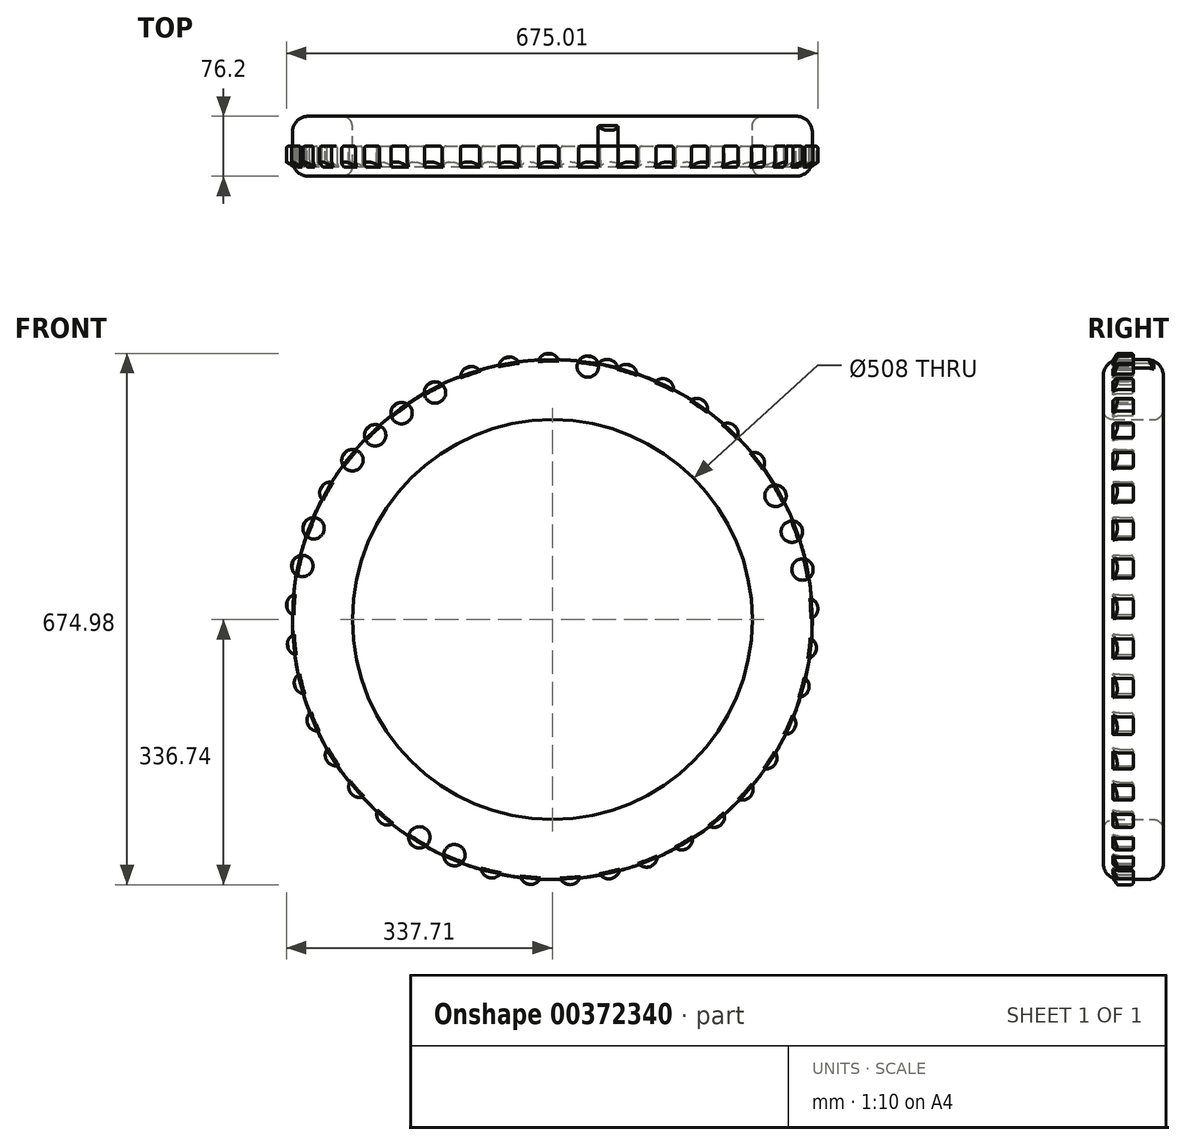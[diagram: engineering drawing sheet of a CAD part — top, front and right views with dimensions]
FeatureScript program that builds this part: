
annotation { "Feature Type Name" : "Feature", "Feature Type Description" : "" }
export const myFeature = defineFeature(function(context is Context, id is Id, definition is map)
    precondition{}
    {
        {
            var Q0;
            Q0=qCreatedBy(makeId("Front.planeOp"),FACE);
            var sketch = newSketch(context, id + "F0", { "sketchPlane" : qUnion([Q0])});
            skCircle(sketch, "E0", {"center": v(0, 0) * mm, "radius": 330.2 * mm});
            skCircle(sketch, "E1", {"center": v(0, 0) * mm, "radius": 254 * mm});
            skSolve(sketch);
        }
        {
            var Q0;
            Q0 = qSketchRegion(id + "F0", true);
            extrude(context, id + "F1", {"entities" : qUnion([Q0]), "endBound" : BoundingType.SYMMETRIC, "depth" : 76.2 * mm});
        }
        {
            var Q0;
            Q0=makeQuery(id+"F1.opExtrude","CAP_EDGE",EDGE,{"disambiguationData":[OSD([sQuery(id+"F0.wireOp",EDGE,"E0")])],"isStart":false});
            var Q1;
            Q1=makeQuery(id+"F1.opExtrude","CAP_EDGE",EDGE,{"disambiguationData":[OSD([sQuery(id+"F0.wireOp",EDGE,"E0")])],"isStart":true});
            fillet(context, id + "F2", {"entities" : qUnion([Q0, Q1]), "radius" : 20.32 * mm, "tangentPropagation" : true, "allowEdgeOverflow" : false});
        }
        {
            var Q0;
            Q0=qCreatedBy(makeId("Front.planeOp"),FACE);
            var sketch = newSketch(context, id + "F3", { "sketchPlane" : qUnion([Q0])});
            skLineSegment(sketch, "E2", {"start": v(-204.7, 258.7) * mm, "end": v(-200.7, 257.56) * mm});
            skLineSegment(sketch, "E3.MirrorCS", {"start": v(-184.2, 273.67) * mm, "end": v(-184.34, 269.52) * mm});
            skLineSegment(sketch, "E4", {"start": v(-184.34, 269.52) * mm, "end": v(-200.7, 257.56) * mm});
            skArc(sketch, "E5", {"start": v(-184.2, 273.67) * mm, "mid": v(-199.59, 273.22) * mm, "end": v(-204.7, 258.7) * mm});
            skLineSegment(sketch, "E6.MirrorCS", {"start": v(-158.8, 285.3) * mm, "end": v(-140.8, 294.6) * mm});
            skLineSegment(sketch, "E7.MirrorCS", {"start": v(-162.58, 287.04) * mm, "end": v(-158.8, 285.3) * mm});
            skArc(sketch, "E8.MirrorCS", {"start": v(-162.58, 287.04) * mm, "mid": v(-155.3, 300.6) * mm, "end": v(-140.03, 298.69) * mm});
            skLineSegment(sketch, "E9.MirrorCS", {"start": v(-140.03, 298.69) * mm, "end": v(-140.8, 294.6) * mm});
            skArc(sketch, "E10.MirrorCS", {"start": v(-92.54, 316.62) * mm, "mid": v(-107.34, 320.86) * mm, "end": v(-116.6, 308.58) * mm});
            skLineSegment(sketch, "E11.MirrorCS", {"start": v(-116.6, 308.58) * mm, "end": v(-113.14, 306.28) * mm});
            skLineSegment(sketch, "E12.MirrorCS", {"start": v(-93.93, 312.7) * mm, "end": v(-113.14, 306.28) * mm});
            skLineSegment(sketch, "E13.MirrorCS", {"start": v(-92.54, 316.62) * mm, "end": v(-93.93, 312.7) * mm});
            skLineSegment(sketch, "E14.MirrorCS", {"start": v(-64.8, 320) * mm, "end": v(-44.83, 323.38) * mm});
            skArc(sketch, "E15.MirrorCS", {"start": v(-67.88, 322.8) * mm, "mid": v(-56.82, 333.5) * mm, "end": v(-42.86, 327.04) * mm});
            skLineSegment(sketch, "E16.MirrorCS", {"start": v(-67.88, 322.8) * mm, "end": v(-64.8, 320) * mm});
            skLineSegment(sketch, "E17.MirrorCS", {"start": v(-42.86, 327.04) * mm, "end": v(-44.83, 323.38) * mm});
            skArc(sketch, "E18.MirrorCS", {"start": v(7.84, 329.7) * mm, "mid": v(-4.97, 338.24) * mm, "end": v(-17.54, 329.35) * mm});
            skLineSegment(sketch, "E19.MirrorCS", {"start": v(5.32, 326.4) * mm, "end": v(-14.93, 326.11) * mm});
            skLineSegment(sketch, "E20.MirrorCS", {"start": v(-17.54, 329.35) * mm, "end": v(-14.93, 326.11) * mm});
            skLineSegment(sketch, "E21.MirrorCS", {"start": v(7.84, 329.7) * mm, "end": v(5.32, 326.4) * mm});
            skArc(sketch, "E22.MirrorCS", {"start": v(33.21, 328.1) * mm, "mid": v(47, 334.94) * mm, "end": v(58.34, 324.54) * mm});
            skLineSegment(sketch, "E23.MirrorCS", {"start": v(58.34, 324.54) * mm, "end": v(55.35, 321.65) * mm});
            skLineSegment(sketch, "E24.MirrorCS", {"start": v(35.29, 324.49) * mm, "end": v(55.35, 321.65) * mm});
            skLineSegment(sketch, "E25.MirrorCS", {"start": v(33.21, 328.1) * mm, "end": v(35.29, 324.49) * mm});
            skArc(sketch, "E26.MirrorCS", {"start": v(107.45, 311.67) * mm, "mid": v(97.84, 323.7) * mm, "end": v(83.17, 319.05) * mm});
            skLineSegment(sketch, "E27.MirrorCS", {"start": v(104.05, 309.28) * mm, "end": v(84.66, 315.17) * mm});
            skLineSegment(sketch, "E28.MirrorCS", {"start": v(83.17, 319.05) * mm, "end": v(84.66, 315.17) * mm});
            skLineSegment(sketch, "E29.MirrorCS", {"start": v(107.45, 311.67) * mm, "end": v(104.05, 309.28) * mm});
            skArc(sketch, "E30.MirrorCS", {"start": v(131.14, 302.43) * mm, "mid": v(146.35, 304.77) * mm, "end": v(154, 291.42) * mm});
            skArc(sketch, "E31.MirrorCS", {"start": v(196.87, 264.24) * mm, "mid": v(191.37, 278.62) * mm, "end": v(175.98, 278.64) * mm});
            skArc(sketch, "E32.MirrorCS", {"start": v(216.64, 248.24) * mm, "mid": v(231.84, 245.85) * mm, "end": v(235.07, 230.8) * mm});
            skLineSegment(sketch, "E33.MirrorCS", {"start": v(216.24, 244.1) * mm, "end": v(230.96, 230.18) * mm});
            skLineSegment(sketch, "E34.MirrorCS", {"start": v(192.9, 263) * mm, "end": v(176.23, 274.5) * mm});
            skLineSegment(sketch, "E35.MirrorCS", {"start": v(132.02, 298.37) * mm, "end": v(150.27, 289.57) * mm});
            skLineSegment(sketch, "E36.MirrorCS", {"start": v(235.07, 230.8) * mm, "end": v(230.96, 230.18) * mm});
            skLineSegment(sketch, "E37.MirrorCS", {"start": v(216.64, 248.24) * mm, "end": v(216.24, 244.1) * mm});
            skLineSegment(sketch, "E38.MirrorCS", {"start": v(196.87, 264.24) * mm, "end": v(192.9, 263) * mm});
            skLineSegment(sketch, "E39.MirrorCS", {"start": v(175.98, 278.64) * mm, "end": v(176.23, 274.5) * mm});
            skLineSegment(sketch, "E40.MirrorCS", {"start": v(154, 291.42) * mm, "end": v(150.27, 289.57) * mm});
            skLineSegment(sketch, "E41.MirrorCS", {"start": v(131.14, 302.43) * mm, "end": v(132.02, 298.37) * mm});
            skLineSegment(sketch, "E42.MirrorCS", {"start": v(249.43, -209.24) * mm, "end": v(235.92, -224.34) * mm});
            skArc(sketch, "E43.MirrorCS", {"start": v(253.57, -209.51) * mm, "mid": v(251.61, -224.78) * mm, "end": v(236.66, -228.43) * mm});
            skLineSegment(sketch, "E44.MirrorCS", {"start": v(236.66, -228.43) * mm, "end": v(235.92, -224.34) * mm});
            skLineSegment(sketch, "E45.MirrorCS", {"start": v(253.57, -209.51) * mm, "end": v(249.43, -209.24) * mm});
            skArc(sketch, "E46.MirrorCS", {"start": v(269.01, -189.3) * mm, "mid": v(283.22, -183.4) * mm, "end": v(282.82, -168.02) * mm});
            skLineSegment(sketch, "E47.MirrorCS", {"start": v(267.65, -185.38) * mm, "end": v(278.68, -168.38) * mm});
            skLineSegment(sketch, "E48.MirrorCS", {"start": v(269.01, -189.3) * mm, "end": v(267.65, -185.38) * mm});
            skLineSegment(sketch, "E49.MirrorCS", {"start": v(282.82, -168.02) * mm, "end": v(278.68, -168.38) * mm});
            skArc(sketch, "E50.MirrorCS", {"start": v(305.33, -122.52) * mm, "mid": v(308.1, -137.66) * mm, "end": v(294.96, -145.68) * mm});
            skLineSegment(sketch, "E51.MirrorCS", {"start": v(301.3, -123.52) * mm, "end": v(293.02, -142) * mm});
            skLineSegment(sketch, "E52.MirrorCS", {"start": v(305.33, -122.52) * mm, "end": v(301.3, -123.52) * mm});
            skLineSegment(sketch, "E53.MirrorCS", {"start": v(294.96, -145.68) * mm, "end": v(293.02, -142) * mm});
            skArc(sketch, "E54.MirrorCS", {"start": v(313.9, -98.58) * mm, "mid": v(325.65, -88.64) * mm, "end": v(320.6, -74.1) * mm});
            skArc(sketch, "E55.MirrorCS", {"start": v(328.22, -23.92) * mm, "mid": v(335.46, -37.5) * mm, "end": v(325.38, -49.13) * mm});
            skArc(sketch, "E56.MirrorCS", {"start": v(329.12, 1.5) * mm, "mid": v(337.29, 14.54) * mm, "end": v(328.05, 26.85) * mm});
            skArc(sketch, "E57.MirrorCS", {"start": v(320.08, 76.98) * mm, "mid": v(331.1, 66.24) * mm, "end": v(325.03, 52.1) * mm});
            skLineSegment(sketch, "E58.MirrorCS", {"start": v(325.03, 52.1) * mm, "end": v(321.32, 53.97) * mm});
            skLineSegment(sketch, "E59.MirrorCS", {"start": v(317.37, 73.84) * mm, "end": v(321.32, 53.97) * mm});
            skLineSegment(sketch, "E60.MirrorCS", {"start": v(311.42, -95.25) * mm, "end": v(316.76, -75.7) * mm});
            skLineSegment(sketch, "E61.MirrorCS", {"start": v(320.6, -74.1) * mm, "end": v(316.76, -75.7) * mm});
            skLineSegment(sketch, "E62.MirrorCS", {"start": v(313.9, -98.58) * mm, "end": v(311.42, -95.25) * mm});
            skLineSegment(sketch, "E63.MirrorCS", {"start": v(325.38, -49.13) * mm, "end": v(322.41, -46.22) * mm});
            skLineSegment(sketch, "E64.MirrorCS", {"start": v(324.68, -26.1) * mm, "end": v(322.41, -46.22) * mm});
            skLineSegment(sketch, "E65.MirrorCS", {"start": v(328.22, -23.92) * mm, "end": v(324.68, -26.1) * mm});
            skLineSegment(sketch, "E66.MirrorCS", {"start": v(328.05, 26.85) * mm, "end": v(324.89, 24.16) * mm});
            skLineSegment(sketch, "E67.MirrorCS", {"start": v(320.08, 76.98) * mm, "end": v(317.37, 73.84) * mm});
            skArc(sketch, "E68.MirrorCS", {"start": v(313.22, 101.47) * mm, "mid": v(317.04, 116.37) * mm, "end": v(304.5, 125.3) * mm});
            skLineSegment(sketch, "E69.MirrorCS", {"start": v(313.22, 101.47) * mm, "end": v(309.26, 102.74) * mm});
            skLineSegment(sketch, "E70.MirrorCS", {"start": v(309.26, 102.74) * mm, "end": v(302.3, 121.77) * mm});
            skLineSegment(sketch, "E71.MirrorCS", {"start": v(304.5, 125.3) * mm, "end": v(302.3, 121.77) * mm});
            skArc(sketch, "E72.MirrorCS", {"start": v(281.68, 170.64) * mm, "mid": v(295.44, 163.75) * mm, "end": v(293.95, 148.43) * mm});
            skLineSegment(sketch, "E73.MirrorCS", {"start": v(293.95, 148.43) * mm, "end": v(289.85, 149.09) * mm});
            skLineSegment(sketch, "E74.MirrorCS", {"start": v(280.05, 166.82) * mm, "end": v(289.85, 149.09) * mm});
            skLineSegment(sketch, "E75.MirrorCS", {"start": v(281.68, 170.64) * mm, "end": v(280.05, 166.82) * mm});
            skArc(sketch, "E76.MirrorCS", {"start": v(267.7, 191.88) * mm, "mid": v(266.81, 207.25) * mm, "end": v(252.16, 211.94) * mm});
            skLineSegment(sketch, "E77.MirrorCS", {"start": v(252.16, 211.94) * mm, "end": v(251.13, 207.91) * mm});
            skLineSegment(sketch, "E78.MirrorCS", {"start": v(263.54, 191.9) * mm, "end": v(251.13, 207.91) * mm});
            skLineSegment(sketch, "E79.MirrorCS", {"start": v(267.7, 191.88) * mm, "end": v(263.54, 191.9) * mm});
            skArc(sketch, "E80.MirrorCS", {"start": v(-279.9, 174.58) * mm, "mid": v(-293.75, 167.88) * mm, "end": v(-292.48, 152.54) * mm});
            skArc(sketch, "E81.MirrorCS", {"start": v(-265.62, 195.62) * mm, "mid": v(-264.52, 210.97) * mm, "end": v(-249.8, 215.46) * mm});
            skArc(sketch, "E82.MirrorCS", {"start": v(-312.4, 105.85) * mm, "mid": v(-316.01, 120.8) * mm, "end": v(-303.35, 129.55) * mm});
            skArc(sketch, "E83.MirrorCS", {"start": v(-319.6, 81.46) * mm, "mid": v(-330.78, 70.87) * mm, "end": v(-324.9, 56.65) * mm});
            skArc(sketch, "E84.MirrorCS", {"start": v(-329.7, 6.1) * mm, "mid": v(-337.69, 19.26) * mm, "end": v(-328.28, 31.44) * mm});
            skArc(sketch, "E85.MirrorCS", {"start": v(-329.16, -19.31) * mm, "mid": v(-336.58, -32.8) * mm, "end": v(-326.67, -44.56) * mm});
            skArc(sketch, "E86.MirrorCS", {"start": v(-315.89, -94.17) * mm, "mid": v(-327.5, -84.06) * mm, "end": v(-322.23, -69.6) * mm});
            skArc(sketch, "E87.MirrorCS", {"start": v(-307.65, -118.23) * mm, "mid": v(-310.63, -133.33) * mm, "end": v(-297.61, -141.53) * mm});
            skArc(sketch, "E88.MirrorCS", {"start": v(-272.27, -185.52) * mm, "mid": v(-286.4, -179.41) * mm, "end": v(-285.78, -164.04) * mm});
            skArc(sketch, "E89.MirrorCS", {"start": v(-257.12, -205.94) * mm, "mid": v(-255.37, -221.23) * mm, "end": v(-240.47, -225.1) * mm});
            skArc(sketch, "E90.MirrorCS", {"start": v(-202.96, -259.33) * mm, "mid": v(-218.28, -257.8) * mm, "end": v(-222.35, -242.96) * mm});
            skArc(sketch, "E91.MirrorCS", {"start": v(-182.33, -274.2) * mm, "mid": v(-176.03, -288.23) * mm, "end": v(-160.66, -287.4) * mm});
            skArc(sketch, "E92.MirrorCS", {"start": v(-114.54, -308.62) * mm, "mid": v(-129.6, -311.81) * mm, "end": v(-137.99, -298.9) * mm});
            skArc(sketch, "E93.MirrorCS", {"start": v(-90.37, -316.51) * mm, "mid": v(-80.1, -327.98) * mm, "end": v(-65.72, -322.5) * mm});
            skArc(sketch, "E94.MirrorCS", {"start": v(-15.33, -328.73) * mm, "mid": v(-28.7, -336.34) * mm, "end": v(-40.62, -326.6) * mm});
            skArc(sketch, "E95.MirrorCS", {"start": v(10.1, -328.9) * mm, "mid": v(23.36, -336.7) * mm, "end": v(35.4, -327.12) * mm});
            skArc(sketch, "E96.MirrorCS", {"start": v(85.3, -317.74) * mm, "mid": v(74.87, -329.06) * mm, "end": v(60.56, -323.4) * mm});
            skArc(sketch, "E97.MirrorCS", {"start": v(109.58, -310.2) * mm, "mid": v(124.59, -313.6) * mm, "end": v(133.15, -300.8) * mm});
            skArc(sketch, "E98.MirrorCS", {"start": v(177.84, -276.72) * mm, "mid": v(171.34, -290.67) * mm, "end": v(155.98, -289.61) * mm});
            skArc(sketch, "E99.MirrorCS", {"start": v(198.68, -262.15) * mm, "mid": v(214, -260.83) * mm, "end": v(218.29, -246.04) * mm});
            skLineSegment(sketch, "E100.MirrorCS", {"start": v(329.12, 1.5) * mm, "end": v(325.74, 3.91) * mm});
            skLineSegment(sketch, "E101", {"start": v(324.89, 24.16) * mm, "end": v(325.74, 3.91) * mm});
            skArc(sketch, "E102.MirrorCS", {"start": v(-237.61, 228.84) * mm, "mid": v(-234.5, 243.91) * mm, "end": v(-219.32, 246.42) * mm});
            skLineSegment(sketch, "E103.MirrorCS", {"start": v(-233.5, 228.25) * mm, "end": v(-218.9, 242.29) * mm});
            skLineSegment(sketch, "E104.MirrorCS", {"start": v(-237.61, 228.84) * mm, "end": v(-233.5, 228.25) * mm});
            skLineSegment(sketch, "E105.MirrorCS", {"start": v(-219.32, 246.42) * mm, "end": v(-218.9, 242.29) * mm});
            skLineSegment(sketch, "E106.MirrorCS", {"start": v(-265.62, 195.62) * mm, "end": v(-261.46, 195.58) * mm});
            skLineSegment(sketch, "E107.MirrorCS", {"start": v(-261.46, 195.58) * mm, "end": v(-248.83, 211.41) * mm});
            skLineSegment(sketch, "E108.MirrorCS", {"start": v(-249.8, 215.46) * mm, "end": v(-248.83, 211.41) * mm});
            skLineSegment(sketch, "E109.MirrorCS", {"start": v(-292.48, 152.54) * mm, "end": v(-288.37, 153.14) * mm});
            skLineSegment(sketch, "E110.MirrorCS", {"start": v(-278.32, 170.73) * mm, "end": v(-288.37, 153.14) * mm});
            skLineSegment(sketch, "E111.MirrorCS", {"start": v(-279.9, 174.58) * mm, "end": v(-278.32, 170.73) * mm});
            skLineSegment(sketch, "E112.MirrorCS", {"start": v(-303.35, 129.55) * mm, "end": v(-301.2, 126) * mm});
            skLineSegment(sketch, "E113.MirrorCS", {"start": v(-308.43, 107.07) * mm, "end": v(-301.2, 126) * mm});
            skLineSegment(sketch, "E114.MirrorCS", {"start": v(-312.4, 105.85) * mm, "end": v(-308.43, 107.07) * mm});
            skLineSegment(sketch, "E115.MirrorCS", {"start": v(-319.6, 81.46) * mm, "end": v(-316.94, 78.28) * mm});
            skLineSegment(sketch, "E116.MirrorCS", {"start": v(-316.94, 78.28) * mm, "end": v(-321.17, 58.47) * mm});
            skLineSegment(sketch, "E117.MirrorCS", {"start": v(-324.9, 56.65) * mm, "end": v(-321.17, 58.47) * mm});
            skLineSegment(sketch, "E118.MirrorCS", {"start": v(-328.28, 31.44) * mm, "end": v(-325.15, 28.7) * mm});
            skLineSegment(sketch, "E119.MirrorCS", {"start": v(-326.29, 8.48) * mm, "end": v(-325.15, 28.7) * mm});
            skLineSegment(sketch, "E120.MirrorCS", {"start": v(-329.7, 6.1) * mm, "end": v(-326.29, 8.48) * mm});
            skLineSegment(sketch, "E121.MirrorCS", {"start": v(-329.16, -19.31) * mm, "end": v(-325.65, -21.54) * mm});
            skLineSegment(sketch, "E122.MirrorCS", {"start": v(-325.65, -21.54) * mm, "end": v(-323.66, -41.7) * mm});
            skLineSegment(sketch, "E123.MirrorCS", {"start": v(-326.67, -44.56) * mm, "end": v(-323.66, -41.7) * mm});
            skLineSegment(sketch, "E124.MirrorCS", {"start": v(-322.23, -69.6) * mm, "end": v(-318.42, -71.26) * mm});
            skLineSegment(sketch, "E125.MirrorCS", {"start": v(-313.36, -90.88) * mm, "end": v(-318.42, -71.26) * mm});
            skLineSegment(sketch, "E126.MirrorCS", {"start": v(-315.89, -94.17) * mm, "end": v(-313.36, -90.88) * mm});
            skLineSegment(sketch, "E127.MirrorCS", {"start": v(-307.65, -118.23) * mm, "end": v(-303.63, -119.28) * mm});
            skLineSegment(sketch, "E128.MirrorCS", {"start": v(-303.63, -119.28) * mm, "end": v(-295.61, -137.89) * mm});
            skLineSegment(sketch, "E129.MirrorCS", {"start": v(-297.61, -141.53) * mm, "end": v(-295.61, -137.89) * mm});
            skLineSegment(sketch, "E130.MirrorCS", {"start": v(-285.78, -164.04) * mm, "end": v(-281.64, -164.46) * mm});
            skLineSegment(sketch, "E131.MirrorCS", {"start": v(-270.86, -181.6) * mm, "end": v(-281.64, -164.46) * mm});
            skLineSegment(sketch, "E132.MirrorCS", {"start": v(-272.27, -185.52) * mm, "end": v(-270.86, -181.6) * mm});
            skLineSegment(sketch, "E133.MirrorCS", {"start": v(-257.12, -205.94) * mm, "end": v(-252.97, -205.72) * mm});
            skLineSegment(sketch, "E134.MirrorCS", {"start": v(-252.97, -205.72) * mm, "end": v(-239.68, -221) * mm});
            skLineSegment(sketch, "E135.MirrorCS", {"start": v(-240.47, -225.1) * mm, "end": v(-239.68, -221) * mm});
            skLineSegment(sketch, "E136.MirrorCS", {"start": v(-222.35, -242.96) * mm, "end": v(-218.28, -242.1) * mm});
            skLineSegment(sketch, "E137.MirrorCS", {"start": v(-202.8, -255.18) * mm, "end": v(-218.28, -242.1) * mm});
            skLineSegment(sketch, "E138.MirrorCS", {"start": v(-202.96, -259.33) * mm, "end": v(-202.8, -255.18) * mm});
            skLineSegment(sketch, "E139.MirrorCS", {"start": v(-182.33, -274.2) * mm, "end": v(-178.44, -272.73) * mm});
            skLineSegment(sketch, "E140.MirrorCS", {"start": v(-178.44, -272.73) * mm, "end": v(-161.14, -283.27) * mm});
            skLineSegment(sketch, "E141.MirrorCS", {"start": v(-160.66, -287.4) * mm, "end": v(-161.14, -283.27) * mm});
            skLineSegment(sketch, "E142.MirrorCS", {"start": v(-137.99, -298.9) * mm, "end": v(-134.37, -296.86) * mm});
            skLineSegment(sketch, "E143.MirrorCS", {"start": v(-115.65, -304.62) * mm, "end": v(-134.37, -296.86) * mm});
            skLineSegment(sketch, "E144.MirrorCS", {"start": v(-114.54, -308.62) * mm, "end": v(-115.65, -304.62) * mm});
            skLineSegment(sketch, "E145.MirrorCS", {"start": v(-90.37, -316.51) * mm, "end": v(-87.11, -313.94) * mm});
            skLineSegment(sketch, "E146.MirrorCS", {"start": v(-87.11, -313.94) * mm, "end": v(-67.43, -318.72) * mm});
            skLineSegment(sketch, "E147.MirrorCS", {"start": v(-65.72, -322.5) * mm, "end": v(-67.43, -318.72) * mm});
            skLineSegment(sketch, "E148.MirrorCS", {"start": v(-40.62, -326.6) * mm, "end": v(-37.8, -323.54) * mm});
            skLineSegment(sketch, "E149.MirrorCS", {"start": v(-37.8, -323.54) * mm, "end": v(-17.6, -325.25) * mm});
            skLineSegment(sketch, "E150.MirrorCS", {"start": v(-15.33, -328.73) * mm, "end": v(-17.6, -325.25) * mm});
            skLineSegment(sketch, "E151.MirrorCS", {"start": v(10.1, -328.9) * mm, "end": v(12.42, -325.46) * mm});
            skLineSegment(sketch, "E152.MirrorCS", {"start": v(12.42, -325.46) * mm, "end": v(32.63, -324.04) * mm});
            skLineSegment(sketch, "E153.MirrorCS", {"start": v(35.4, -327.12) * mm, "end": v(32.63, -324.04) * mm});
            skLineSegment(sketch, "E154.MirrorCS", {"start": v(60.56, -323.4) * mm, "end": v(62.32, -319.63) * mm});
            skLineSegment(sketch, "E155.MirrorCS", {"start": v(82.07, -315.12) * mm, "end": v(62.32, -319.63) * mm});
            skLineSegment(sketch, "E156.MirrorCS", {"start": v(85.3, -317.74) * mm, "end": v(82.07, -315.12) * mm});
            skLineSegment(sketch, "E157.MirrorCS", {"start": v(109.58, -310.2) * mm, "end": v(110.74, -306.2) * mm});
            skLineSegment(sketch, "E158.MirrorCS", {"start": v(110.74, -306.2) * mm, "end": v(129.56, -298.7) * mm});
            skLineSegment(sketch, "E159.MirrorCS", {"start": v(133.15, -300.8) * mm, "end": v(129.56, -298.7) * mm});
            skLineSegment(sketch, "E160.MirrorCS", {"start": v(155.98, -289.61) * mm, "end": v(156.52, -285.5) * mm});
            skLineSegment(sketch, "E161.MirrorCS", {"start": v(173.97, -275.2) * mm, "end": v(156.52, -285.5) * mm});
            skLineSegment(sketch, "E162.MirrorCS", {"start": v(177.84, -276.72) * mm, "end": v(173.97, -275.2) * mm});
            skLineSegment(sketch, "E163.MirrorCS", {"start": v(198.68, -262.15) * mm, "end": v(198.57, -257.99) * mm});
            skLineSegment(sketch, "E164.MirrorCS", {"start": v(198.57, -257.99) * mm, "end": v(214.23, -245.14) * mm});
            skLineSegment(sketch, "E165.MirrorCS", {"start": v(218.29, -246.04) * mm, "end": v(214.23, -245.14) * mm});
            skSolve(sketch);
        }
        {
            var Q0;
            Q0 = qSketchRegion(id + "F3", true);
            extrude(context, id + "F4", {"entities" : qUnion([Q0]), "operationType" : NewBodyOperationType.ADD, "depth" : 20.32 * mm});
        }
        {
            var Q0;
            {var subQ0=sQuery(id+"F0.wireOp",EDGE,"E0");Q0=makeQuery(id+"F4.boolean.opBoolean","INTERSECT",EDGE,{"derivedFrom":[makeQuery(id+"F2.opFillet","BLEND_FACE",FACE,{"disambiguationData":[OSD([subQ0]),TDD([makeQuery(id+"F1.opExtrude","CAP_EDGE",EDGE,{"disambiguationData":[OSD([subQ0])],"isStart":false})])]}),makeQuery(id+"F4.opExtrude","CAP_FACE",FACE,{"disambiguationData":[OSD([sQuery(id+"F3.wireOp",EDGE,"E2"),sQuery(id+"F3.wireOp",EDGE,"E3.MirrorCS"),sQuery(id+"F3.wireOp",EDGE,"E4"),sQuery(id+"F3.wireOp",EDGE,"E5")])],"isStart":false})]});}
            var Q1;
            {var subQ0=sQuery(id+"F0.wireOp",EDGE,"E0");Q1=makeQuery(id+"F4.boolean.opBoolean","INTERSECT",EDGE,{"derivedFrom":[makeQuery(id+"F2.opFillet","BLEND_FACE",FACE,{"disambiguationData":[OSD([subQ0]),TDD([makeQuery(id+"F1.opExtrude","CAP_EDGE",EDGE,{"disambiguationData":[OSD([subQ0])],"isStart":false})])]}),makeQuery(id+"F4.opExtrude","CAP_FACE",FACE,{"disambiguationData":[OSD([sQuery(id+"F3.wireOp",EDGE,"E6.MirrorCS"),sQuery(id+"F3.wireOp",EDGE,"E7.MirrorCS"),sQuery(id+"F3.wireOp",EDGE,"E8.MirrorCS"),sQuery(id+"F3.wireOp",EDGE,"E9.MirrorCS")])],"isStart":false})]});}
            var Q2;
            {var subQ0=sQuery(id+"F0.wireOp",EDGE,"E0");Q2=makeQuery(id+"F4.boolean.opBoolean","INTERSECT",EDGE,{"derivedFrom":[makeQuery(id+"F2.opFillet","BLEND_FACE",FACE,{"disambiguationData":[OSD([subQ0]),TDD([makeQuery(id+"F1.opExtrude","CAP_EDGE",EDGE,{"disambiguationData":[OSD([subQ0])],"isStart":false})])]}),makeQuery(id+"F4.opExtrude","CAP_FACE",FACE,{"disambiguationData":[OSD([sQuery(id+"F3.wireOp",EDGE,"E10.MirrorCS"),sQuery(id+"F3.wireOp",EDGE,"E11.MirrorCS"),sQuery(id+"F3.wireOp",EDGE,"E12.MirrorCS"),sQuery(id+"F3.wireOp",EDGE,"E13.MirrorCS")])],"isStart":false})]});}
            var Q3;
            {var subQ0=sQuery(id+"F0.wireOp",EDGE,"E0");Q3=makeQuery(id+"F4.boolean.opBoolean","INTERSECT",EDGE,{"derivedFrom":[makeQuery(id+"F2.opFillet","BLEND_FACE",FACE,{"disambiguationData":[OSD([subQ0]),TDD([makeQuery(id+"F1.opExtrude","CAP_EDGE",EDGE,{"disambiguationData":[OSD([subQ0])],"isStart":false})])]}),makeQuery(id+"F4.opExtrude","CAP_FACE",FACE,{"disambiguationData":[OSD([sQuery(id+"F3.wireOp",EDGE,"E14.MirrorCS"),sQuery(id+"F3.wireOp",EDGE,"E15.MirrorCS"),sQuery(id+"F3.wireOp",EDGE,"E16.MirrorCS"),sQuery(id+"F3.wireOp",EDGE,"E17.MirrorCS")])],"isStart":false})]});}
            var Q4;
            {var subQ0=sQuery(id+"F0.wireOp",EDGE,"E0");Q4=makeQuery(id+"F4.boolean.opBoolean","INTERSECT",EDGE,{"derivedFrom":[makeQuery(id+"F2.opFillet","BLEND_FACE",FACE,{"disambiguationData":[OSD([subQ0]),TDD([makeQuery(id+"F1.opExtrude","CAP_EDGE",EDGE,{"disambiguationData":[OSD([subQ0])],"isStart":false})])]}),makeQuery(id+"F4.opExtrude","CAP_FACE",FACE,{"disambiguationData":[OSD([sQuery(id+"F3.wireOp",EDGE,"E18.MirrorCS"),sQuery(id+"F3.wireOp",EDGE,"E19.MirrorCS"),sQuery(id+"F3.wireOp",EDGE,"E20.MirrorCS"),sQuery(id+"F3.wireOp",EDGE,"E21.MirrorCS")])],"isStart":false})]});}
            var Q5;
            {var subQ0=sQuery(id+"F0.wireOp",EDGE,"E0");Q5=makeQuery(id+"F4.boolean.opBoolean","INTERSECT",EDGE,{"derivedFrom":[makeQuery(id+"F2.opFillet","BLEND_FACE",FACE,{"disambiguationData":[OSD([subQ0]),TDD([makeQuery(id+"F1.opExtrude","CAP_EDGE",EDGE,{"disambiguationData":[OSD([subQ0])],"isStart":false})])]}),makeQuery(id+"F4.opExtrude","CAP_FACE",FACE,{"disambiguationData":[OSD([sQuery(id+"F3.wireOp",EDGE,"E22.MirrorCS"),sQuery(id+"F3.wireOp",EDGE,"E23.MirrorCS"),sQuery(id+"F3.wireOp",EDGE,"E24.MirrorCS"),sQuery(id+"F3.wireOp",EDGE,"E25.MirrorCS")])],"isStart":false})]});}
            var Q6;
            {var subQ0=sQuery(id+"F0.wireOp",EDGE,"E0");Q6=makeQuery(id+"F4.boolean.opBoolean","INTERSECT",EDGE,{"derivedFrom":[makeQuery(id+"F2.opFillet","BLEND_FACE",FACE,{"disambiguationData":[OSD([subQ0]),TDD([makeQuery(id+"F1.opExtrude","CAP_EDGE",EDGE,{"disambiguationData":[OSD([subQ0])],"isStart":false})])]}),makeQuery(id+"F4.opExtrude","CAP_FACE",FACE,{"disambiguationData":[OSD([sQuery(id+"F3.wireOp",EDGE,"E26.MirrorCS"),sQuery(id+"F3.wireOp",EDGE,"E27.MirrorCS"),sQuery(id+"F3.wireOp",EDGE,"E28.MirrorCS"),sQuery(id+"F3.wireOp",EDGE,"E29.MirrorCS")])],"isStart":false})]});}
            var Q7;
            {var subQ0=sQuery(id+"F0.wireOp",EDGE,"E0");Q7=makeQuery(id+"F4.boolean.opBoolean","INTERSECT",EDGE,{"derivedFrom":[makeQuery(id+"F2.opFillet","BLEND_FACE",FACE,{"disambiguationData":[OSD([subQ0]),TDD([makeQuery(id+"F1.opExtrude","CAP_EDGE",EDGE,{"disambiguationData":[OSD([subQ0])],"isStart":false})])]}),makeQuery(id+"F4.opExtrude","CAP_FACE",FACE,{"disambiguationData":[OSD([sQuery(id+"F3.wireOp",EDGE,"E30.MirrorCS"),sQuery(id+"F3.wireOp",EDGE,"E35.MirrorCS"),sQuery(id+"F3.wireOp",EDGE,"E40.MirrorCS"),sQuery(id+"F3.wireOp",EDGE,"E41.MirrorCS")])],"isStart":false})]});}
            var Q8;
            {var subQ0=sQuery(id+"F0.wireOp",EDGE,"E0");Q8=makeQuery(id+"F4.boolean.opBoolean","INTERSECT",EDGE,{"derivedFrom":[makeQuery(id+"F2.opFillet","BLEND_FACE",FACE,{"disambiguationData":[OSD([subQ0]),TDD([makeQuery(id+"F1.opExtrude","CAP_EDGE",EDGE,{"disambiguationData":[OSD([subQ0])],"isStart":false})])]}),makeQuery(id+"F4.opExtrude","CAP_FACE",FACE,{"disambiguationData":[OSD([sQuery(id+"F3.wireOp",EDGE,"E31.MirrorCS"),sQuery(id+"F3.wireOp",EDGE,"E34.MirrorCS"),sQuery(id+"F3.wireOp",EDGE,"E38.MirrorCS"),sQuery(id+"F3.wireOp",EDGE,"E39.MirrorCS")])],"isStart":false})]});}
            var Q9;
            {var subQ0=sQuery(id+"F0.wireOp",EDGE,"E0");Q9=makeQuery(id+"F4.boolean.opBoolean","INTERSECT",EDGE,{"derivedFrom":[makeQuery(id+"F2.opFillet","BLEND_FACE",FACE,{"disambiguationData":[OSD([subQ0]),TDD([makeQuery(id+"F1.opExtrude","CAP_EDGE",EDGE,{"disambiguationData":[OSD([subQ0])],"isStart":false})])]}),makeQuery(id+"F4.opExtrude","CAP_FACE",FACE,{"disambiguationData":[OSD([sQuery(id+"F3.wireOp",EDGE,"E32.MirrorCS"),sQuery(id+"F3.wireOp",EDGE,"E33.MirrorCS"),sQuery(id+"F3.wireOp",EDGE,"E36.MirrorCS"),sQuery(id+"F3.wireOp",EDGE,"E37.MirrorCS")])],"isStart":false})]});}
            var Q10;
            {var subQ0=sQuery(id+"F0.wireOp",EDGE,"E0");Q10=makeQuery(id+"F4.boolean.opBoolean","INTERSECT",EDGE,{"derivedFrom":[makeQuery(id+"F2.opFillet","BLEND_FACE",FACE,{"disambiguationData":[OSD([subQ0]),TDD([makeQuery(id+"F1.opExtrude","CAP_EDGE",EDGE,{"disambiguationData":[OSD([subQ0])],"isStart":false})])]}),makeQuery(id+"F4.opExtrude","CAP_FACE",FACE,{"disambiguationData":[OSD([sQuery(id+"F3.wireOp",EDGE,"E76.MirrorCS"),sQuery(id+"F3.wireOp",EDGE,"E77.MirrorCS"),sQuery(id+"F3.wireOp",EDGE,"E78.MirrorCS"),sQuery(id+"F3.wireOp",EDGE,"E79.MirrorCS")])],"isStart":false})]});}
            var Q11;
            {var subQ0=sQuery(id+"F0.wireOp",EDGE,"E0");Q11=makeQuery(id+"F4.boolean.opBoolean","INTERSECT",EDGE,{"derivedFrom":[makeQuery(id+"F2.opFillet","BLEND_FACE",FACE,{"disambiguationData":[OSD([subQ0]),TDD([makeQuery(id+"F1.opExtrude","CAP_EDGE",EDGE,{"disambiguationData":[OSD([subQ0])],"isStart":false})])]}),makeQuery(id+"F4.opExtrude","CAP_FACE",FACE,{"disambiguationData":[OSD([sQuery(id+"F3.wireOp",EDGE,"E72.MirrorCS"),sQuery(id+"F3.wireOp",EDGE,"E73.MirrorCS"),sQuery(id+"F3.wireOp",EDGE,"E74.MirrorCS"),sQuery(id+"F3.wireOp",EDGE,"E75.MirrorCS")])],"isStart":false})]});}
            var Q12;
            {var subQ0=sQuery(id+"F0.wireOp",EDGE,"E0");Q12=makeQuery(id+"F4.boolean.opBoolean","INTERSECT",EDGE,{"derivedFrom":[makeQuery(id+"F2.opFillet","BLEND_FACE",FACE,{"disambiguationData":[OSD([subQ0]),TDD([makeQuery(id+"F1.opExtrude","CAP_EDGE",EDGE,{"disambiguationData":[OSD([subQ0])],"isStart":false})])]}),makeQuery(id+"F4.opExtrude","CAP_FACE",FACE,{"disambiguationData":[OSD([sQuery(id+"F3.wireOp",EDGE,"E68.MirrorCS"),sQuery(id+"F3.wireOp",EDGE,"E69.MirrorCS"),sQuery(id+"F3.wireOp",EDGE,"E70.MirrorCS"),sQuery(id+"F3.wireOp",EDGE,"E71.MirrorCS")])],"isStart":false})]});}
            var Q13;
            {var subQ0=sQuery(id+"F0.wireOp",EDGE,"E0");Q13=makeQuery(id+"F4.boolean.opBoolean","INTERSECT",EDGE,{"derivedFrom":[makeQuery(id+"F2.opFillet","BLEND_FACE",FACE,{"disambiguationData":[OSD([subQ0]),TDD([makeQuery(id+"F1.opExtrude","CAP_EDGE",EDGE,{"disambiguationData":[OSD([subQ0])],"isStart":false})])]}),makeQuery(id+"F4.opExtrude","CAP_FACE",FACE,{"disambiguationData":[OSD([sQuery(id+"F3.wireOp",EDGE,"E57.MirrorCS"),sQuery(id+"F3.wireOp",EDGE,"E58.MirrorCS"),sQuery(id+"F3.wireOp",EDGE,"E59.MirrorCS"),sQuery(id+"F3.wireOp",EDGE,"E67.MirrorCS")])],"isStart":false})]});}
            var Q14;
            {var subQ0=sQuery(id+"F0.wireOp",EDGE,"E0");Q14=makeQuery(id+"F4.boolean.opBoolean","INTERSECT",EDGE,{"derivedFrom":[makeQuery(id+"F2.opFillet","BLEND_FACE",FACE,{"disambiguationData":[OSD([subQ0]),TDD([makeQuery(id+"F1.opExtrude","CAP_EDGE",EDGE,{"disambiguationData":[OSD([subQ0])],"isStart":false})])]}),makeQuery(id+"F4.opExtrude","CAP_FACE",FACE,{"disambiguationData":[OSD([sQuery(id+"F3.wireOp",EDGE,"E56.MirrorCS"),sQuery(id+"F3.wireOp",EDGE,"E66.MirrorCS"),sQuery(id+"F3.wireOp",EDGE,"E100.MirrorCS"),sQuery(id+"F3.wireOp",EDGE,"E101")])],"isStart":false})]});}
            var Q15;
            {var subQ0=sQuery(id+"F0.wireOp",EDGE,"E0");Q15=makeQuery(id+"F4.boolean.opBoolean","INTERSECT",EDGE,{"derivedFrom":[makeQuery(id+"F2.opFillet","BLEND_FACE",FACE,{"disambiguationData":[OSD([subQ0]),TDD([makeQuery(id+"F1.opExtrude","CAP_EDGE",EDGE,{"disambiguationData":[OSD([subQ0])],"isStart":false})])]}),makeQuery(id+"F4.opExtrude","CAP_FACE",FACE,{"disambiguationData":[OSD([sQuery(id+"F3.wireOp",EDGE,"E55.MirrorCS"),sQuery(id+"F3.wireOp",EDGE,"E63.MirrorCS"),sQuery(id+"F3.wireOp",EDGE,"E64.MirrorCS"),sQuery(id+"F3.wireOp",EDGE,"E65.MirrorCS")])],"isStart":false})]});}
            var Q16;
            {var subQ0=sQuery(id+"F0.wireOp",EDGE,"E0");Q16=makeQuery(id+"F4.boolean.opBoolean","INTERSECT",EDGE,{"derivedFrom":[makeQuery(id+"F2.opFillet","BLEND_FACE",FACE,{"disambiguationData":[OSD([subQ0]),TDD([makeQuery(id+"F1.opExtrude","CAP_EDGE",EDGE,{"disambiguationData":[OSD([subQ0])],"isStart":false})])]}),makeQuery(id+"F4.opExtrude","CAP_FACE",FACE,{"disambiguationData":[OSD([sQuery(id+"F3.wireOp",EDGE,"E96.MirrorCS"),sQuery(id+"F3.wireOp",EDGE,"E154.MirrorCS"),sQuery(id+"F3.wireOp",EDGE,"E155.MirrorCS"),sQuery(id+"F3.wireOp",EDGE,"E156.MirrorCS")])],"isStart":false})]});}
            var Q17;
            {var subQ0=sQuery(id+"F0.wireOp",EDGE,"E0");Q17=makeQuery(id+"F4.boolean.opBoolean","INTERSECT",EDGE,{"derivedFrom":[makeQuery(id+"F2.opFillet","BLEND_FACE",FACE,{"disambiguationData":[OSD([subQ0]),TDD([makeQuery(id+"F1.opExtrude","CAP_EDGE",EDGE,{"disambiguationData":[OSD([subQ0])],"isStart":false})])]}),makeQuery(id+"F4.opExtrude","CAP_FACE",FACE,{"disambiguationData":[OSD([sQuery(id+"F3.wireOp",EDGE,"E97.MirrorCS"),sQuery(id+"F3.wireOp",EDGE,"E157.MirrorCS"),sQuery(id+"F3.wireOp",EDGE,"E158.MirrorCS"),sQuery(id+"F3.wireOp",EDGE,"E159.MirrorCS")])],"isStart":false})]});}
            var Q18;
            {var subQ0=sQuery(id+"F0.wireOp",EDGE,"E0");Q18=makeQuery(id+"F4.boolean.opBoolean","INTERSECT",EDGE,{"derivedFrom":[makeQuery(id+"F2.opFillet","BLEND_FACE",FACE,{"disambiguationData":[OSD([subQ0]),TDD([makeQuery(id+"F1.opExtrude","CAP_EDGE",EDGE,{"disambiguationData":[OSD([subQ0])],"isStart":false})])]}),makeQuery(id+"F4.opExtrude","CAP_FACE",FACE,{"disambiguationData":[OSD([sQuery(id+"F3.wireOp",EDGE,"E98.MirrorCS"),sQuery(id+"F3.wireOp",EDGE,"E160.MirrorCS"),sQuery(id+"F3.wireOp",EDGE,"E161.MirrorCS"),sQuery(id+"F3.wireOp",EDGE,"E162.MirrorCS")])],"isStart":false})]});}
            var Q19;
            {var subQ0=sQuery(id+"F0.wireOp",EDGE,"E0");Q19=makeQuery(id+"F4.boolean.opBoolean","INTERSECT",EDGE,{"derivedFrom":[makeQuery(id+"F2.opFillet","BLEND_FACE",FACE,{"disambiguationData":[OSD([subQ0]),TDD([makeQuery(id+"F1.opExtrude","CAP_EDGE",EDGE,{"disambiguationData":[OSD([subQ0])],"isStart":false})])]}),makeQuery(id+"F4.opExtrude","CAP_FACE",FACE,{"disambiguationData":[OSD([sQuery(id+"F3.wireOp",EDGE,"E99.MirrorCS"),sQuery(id+"F3.wireOp",EDGE,"E163.MirrorCS"),sQuery(id+"F3.wireOp",EDGE,"E164.MirrorCS"),sQuery(id+"F3.wireOp",EDGE,"E165.MirrorCS")])],"isStart":false})]});}
            var Q20;
            {var subQ0=sQuery(id+"F0.wireOp",EDGE,"E0");Q20=makeQuery(id+"F4.boolean.opBoolean","INTERSECT",EDGE,{"derivedFrom":[makeQuery(id+"F2.opFillet","BLEND_FACE",FACE,{"disambiguationData":[OSD([subQ0]),TDD([makeQuery(id+"F1.opExtrude","CAP_EDGE",EDGE,{"disambiguationData":[OSD([subQ0])],"isStart":false})])]}),makeQuery(id+"F4.opExtrude","CAP_FACE",FACE,{"disambiguationData":[OSD([sQuery(id+"F3.wireOp",EDGE,"E42.MirrorCS"),sQuery(id+"F3.wireOp",EDGE,"E43.MirrorCS"),sQuery(id+"F3.wireOp",EDGE,"E44.MirrorCS"),sQuery(id+"F3.wireOp",EDGE,"E45.MirrorCS")])],"isStart":false})]});}
            var Q21;
            {var subQ0=sQuery(id+"F0.wireOp",EDGE,"E0");Q21=makeQuery(id+"F4.boolean.opBoolean","INTERSECT",EDGE,{"derivedFrom":[makeQuery(id+"F2.opFillet","BLEND_FACE",FACE,{"disambiguationData":[OSD([subQ0]),TDD([makeQuery(id+"F1.opExtrude","CAP_EDGE",EDGE,{"disambiguationData":[OSD([subQ0])],"isStart":false})])]}),makeQuery(id+"F4.opExtrude","CAP_FACE",FACE,{"disambiguationData":[OSD([sQuery(id+"F3.wireOp",EDGE,"E46.MirrorCS"),sQuery(id+"F3.wireOp",EDGE,"E47.MirrorCS"),sQuery(id+"F3.wireOp",EDGE,"E48.MirrorCS"),sQuery(id+"F3.wireOp",EDGE,"E49.MirrorCS")])],"isStart":false})]});}
            var Q22;
            {var subQ0=sQuery(id+"F0.wireOp",EDGE,"E0");Q22=makeQuery(id+"F4.boolean.opBoolean","INTERSECT",EDGE,{"derivedFrom":[makeQuery(id+"F2.opFillet","BLEND_FACE",FACE,{"disambiguationData":[OSD([subQ0]),TDD([makeQuery(id+"F1.opExtrude","CAP_EDGE",EDGE,{"disambiguationData":[OSD([subQ0])],"isStart":false})])]}),makeQuery(id+"F4.opExtrude","CAP_FACE",FACE,{"disambiguationData":[OSD([sQuery(id+"F3.wireOp",EDGE,"E50.MirrorCS"),sQuery(id+"F3.wireOp",EDGE,"E51.MirrorCS"),sQuery(id+"F3.wireOp",EDGE,"E52.MirrorCS"),sQuery(id+"F3.wireOp",EDGE,"E53.MirrorCS")])],"isStart":false})]});}
            var Q23;
            {var subQ0=sQuery(id+"F0.wireOp",EDGE,"E0");Q23=makeQuery(id+"F4.boolean.opBoolean","INTERSECT",EDGE,{"derivedFrom":[makeQuery(id+"F2.opFillet","BLEND_FACE",FACE,{"disambiguationData":[OSD([subQ0]),TDD([makeQuery(id+"F1.opExtrude","CAP_EDGE",EDGE,{"disambiguationData":[OSD([subQ0])],"isStart":false})])]}),makeQuery(id+"F4.opExtrude","CAP_FACE",FACE,{"disambiguationData":[OSD([sQuery(id+"F3.wireOp",EDGE,"E54.MirrorCS"),sQuery(id+"F3.wireOp",EDGE,"E60.MirrorCS"),sQuery(id+"F3.wireOp",EDGE,"E61.MirrorCS"),sQuery(id+"F3.wireOp",EDGE,"E62.MirrorCS")])],"isStart":false})]});}
            var Q24;
            {var subQ0=sQuery(id+"F0.wireOp",EDGE,"E0");Q24=makeQuery(id+"F4.boolean.opBoolean","INTERSECT",EDGE,{"derivedFrom":[makeQuery(id+"F2.opFillet","BLEND_FACE",FACE,{"disambiguationData":[OSD([subQ0]),TDD([makeQuery(id+"F1.opExtrude","CAP_EDGE",EDGE,{"disambiguationData":[OSD([subQ0])],"isStart":false})])]}),makeQuery(id+"F4.opExtrude","CAP_FACE",FACE,{"disambiguationData":[OSD([sQuery(id+"F3.wireOp",EDGE,"E95.MirrorCS"),sQuery(id+"F3.wireOp",EDGE,"E151.MirrorCS"),sQuery(id+"F3.wireOp",EDGE,"E152.MirrorCS"),sQuery(id+"F3.wireOp",EDGE,"E153.MirrorCS")])],"isStart":false})]});}
            var Q25;
            {var subQ0=sQuery(id+"F0.wireOp",EDGE,"E0");Q25=makeQuery(id+"F4.boolean.opBoolean","INTERSECT",EDGE,{"derivedFrom":[makeQuery(id+"F2.opFillet","BLEND_FACE",FACE,{"disambiguationData":[OSD([subQ0]),TDD([makeQuery(id+"F1.opExtrude","CAP_EDGE",EDGE,{"disambiguationData":[OSD([subQ0])],"isStart":false})])]}),makeQuery(id+"F4.opExtrude","CAP_FACE",FACE,{"disambiguationData":[OSD([sQuery(id+"F3.wireOp",EDGE,"E94.MirrorCS"),sQuery(id+"F3.wireOp",EDGE,"E148.MirrorCS"),sQuery(id+"F3.wireOp",EDGE,"E149.MirrorCS"),sQuery(id+"F3.wireOp",EDGE,"E150.MirrorCS")])],"isStart":false})]});}
            var Q26;
            {var subQ0=sQuery(id+"F0.wireOp",EDGE,"E0");Q26=makeQuery(id+"F4.boolean.opBoolean","INTERSECT",EDGE,{"derivedFrom":[makeQuery(id+"F2.opFillet","BLEND_FACE",FACE,{"disambiguationData":[OSD([subQ0]),TDD([makeQuery(id+"F1.opExtrude","CAP_EDGE",EDGE,{"disambiguationData":[OSD([subQ0])],"isStart":false})])]}),makeQuery(id+"F4.opExtrude","CAP_FACE",FACE,{"disambiguationData":[OSD([sQuery(id+"F3.wireOp",EDGE,"E93.MirrorCS"),sQuery(id+"F3.wireOp",EDGE,"E145.MirrorCS"),sQuery(id+"F3.wireOp",EDGE,"E146.MirrorCS"),sQuery(id+"F3.wireOp",EDGE,"E147.MirrorCS")])],"isStart":false})]});}
            var Q27;
            {var subQ0=sQuery(id+"F0.wireOp",EDGE,"E0");Q27=makeQuery(id+"F4.boolean.opBoolean","INTERSECT",EDGE,{"derivedFrom":[makeQuery(id+"F2.opFillet","BLEND_FACE",FACE,{"disambiguationData":[OSD([subQ0]),TDD([makeQuery(id+"F1.opExtrude","CAP_EDGE",EDGE,{"disambiguationData":[OSD([subQ0])],"isStart":false})])]}),makeQuery(id+"F4.opExtrude","CAP_FACE",FACE,{"disambiguationData":[OSD([sQuery(id+"F3.wireOp",EDGE,"E92.MirrorCS"),sQuery(id+"F3.wireOp",EDGE,"E142.MirrorCS"),sQuery(id+"F3.wireOp",EDGE,"E143.MirrorCS"),sQuery(id+"F3.wireOp",EDGE,"E144.MirrorCS")])],"isStart":false})]});}
            var Q28;
            {var subQ0=sQuery(id+"F0.wireOp",EDGE,"E0");Q28=makeQuery(id+"F4.boolean.opBoolean","INTERSECT",EDGE,{"derivedFrom":[makeQuery(id+"F2.opFillet","BLEND_FACE",FACE,{"disambiguationData":[OSD([subQ0]),TDD([makeQuery(id+"F1.opExtrude","CAP_EDGE",EDGE,{"disambiguationData":[OSD([subQ0])],"isStart":false})])]}),makeQuery(id+"F4.opExtrude","CAP_FACE",FACE,{"disambiguationData":[OSD([sQuery(id+"F3.wireOp",EDGE,"E91.MirrorCS"),sQuery(id+"F3.wireOp",EDGE,"E139.MirrorCS"),sQuery(id+"F3.wireOp",EDGE,"E140.MirrorCS"),sQuery(id+"F3.wireOp",EDGE,"E141.MirrorCS")])],"isStart":false})]});}
            var Q29;
            {var subQ0=sQuery(id+"F0.wireOp",EDGE,"E0");Q29=makeQuery(id+"F4.boolean.opBoolean","INTERSECT",EDGE,{"derivedFrom":[makeQuery(id+"F2.opFillet","BLEND_FACE",FACE,{"disambiguationData":[OSD([subQ0]),TDD([makeQuery(id+"F1.opExtrude","CAP_EDGE",EDGE,{"disambiguationData":[OSD([subQ0])],"isStart":false})])]}),makeQuery(id+"F4.opExtrude","CAP_FACE",FACE,{"disambiguationData":[OSD([sQuery(id+"F3.wireOp",EDGE,"E90.MirrorCS"),sQuery(id+"F3.wireOp",EDGE,"E136.MirrorCS"),sQuery(id+"F3.wireOp",EDGE,"E137.MirrorCS"),sQuery(id+"F3.wireOp",EDGE,"E138.MirrorCS")])],"isStart":false})]});}
            var Q30;
            {var subQ0=sQuery(id+"F0.wireOp",EDGE,"E0");Q30=makeQuery(id+"F4.boolean.opBoolean","INTERSECT",EDGE,{"derivedFrom":[makeQuery(id+"F2.opFillet","BLEND_FACE",FACE,{"disambiguationData":[OSD([subQ0]),TDD([makeQuery(id+"F1.opExtrude","CAP_EDGE",EDGE,{"disambiguationData":[OSD([subQ0])],"isStart":false})])]}),makeQuery(id+"F4.opExtrude","CAP_FACE",FACE,{"disambiguationData":[OSD([sQuery(id+"F3.wireOp",EDGE,"E89.MirrorCS"),sQuery(id+"F3.wireOp",EDGE,"E133.MirrorCS"),sQuery(id+"F3.wireOp",EDGE,"E134.MirrorCS"),sQuery(id+"F3.wireOp",EDGE,"E135.MirrorCS")])],"isStart":false})]});}
            var Q31;
            {var subQ0=sQuery(id+"F0.wireOp",EDGE,"E0");Q31=makeQuery(id+"F4.boolean.opBoolean","INTERSECT",EDGE,{"derivedFrom":[makeQuery(id+"F2.opFillet","BLEND_FACE",FACE,{"disambiguationData":[OSD([subQ0]),TDD([makeQuery(id+"F1.opExtrude","CAP_EDGE",EDGE,{"disambiguationData":[OSD([subQ0])],"isStart":false})])]}),makeQuery(id+"F4.opExtrude","CAP_FACE",FACE,{"disambiguationData":[OSD([sQuery(id+"F3.wireOp",EDGE,"E88.MirrorCS"),sQuery(id+"F3.wireOp",EDGE,"E130.MirrorCS"),sQuery(id+"F3.wireOp",EDGE,"E131.MirrorCS"),sQuery(id+"F3.wireOp",EDGE,"E132.MirrorCS")])],"isStart":false})]});}
            var Q32;
            {var subQ0=sQuery(id+"F0.wireOp",EDGE,"E0");Q32=makeQuery(id+"F4.boolean.opBoolean","INTERSECT",EDGE,{"derivedFrom":[makeQuery(id+"F2.opFillet","BLEND_FACE",FACE,{"disambiguationData":[OSD([subQ0]),TDD([makeQuery(id+"F1.opExtrude","CAP_EDGE",EDGE,{"disambiguationData":[OSD([subQ0])],"isStart":false})])]}),makeQuery(id+"F4.opExtrude","CAP_FACE",FACE,{"disambiguationData":[OSD([sQuery(id+"F3.wireOp",EDGE,"E87.MirrorCS"),sQuery(id+"F3.wireOp",EDGE,"E127.MirrorCS"),sQuery(id+"F3.wireOp",EDGE,"E128.MirrorCS"),sQuery(id+"F3.wireOp",EDGE,"E129.MirrorCS")])],"isStart":false})]});}
            var Q33;
            {var subQ0=sQuery(id+"F0.wireOp",EDGE,"E0");Q33=makeQuery(id+"F4.boolean.opBoolean","INTERSECT",EDGE,{"derivedFrom":[makeQuery(id+"F2.opFillet","BLEND_FACE",FACE,{"disambiguationData":[OSD([subQ0]),TDD([makeQuery(id+"F1.opExtrude","CAP_EDGE",EDGE,{"disambiguationData":[OSD([subQ0])],"isStart":false})])]}),makeQuery(id+"F4.opExtrude","CAP_FACE",FACE,{"disambiguationData":[OSD([sQuery(id+"F3.wireOp",EDGE,"E86.MirrorCS"),sQuery(id+"F3.wireOp",EDGE,"E124.MirrorCS"),sQuery(id+"F3.wireOp",EDGE,"E125.MirrorCS"),sQuery(id+"F3.wireOp",EDGE,"E126.MirrorCS")])],"isStart":false})]});}
            var Q34;
            {var subQ0=sQuery(id+"F0.wireOp",EDGE,"E0");Q34=makeQuery(id+"F4.boolean.opBoolean","INTERSECT",EDGE,{"derivedFrom":[makeQuery(id+"F2.opFillet","BLEND_FACE",FACE,{"disambiguationData":[OSD([subQ0]),TDD([makeQuery(id+"F1.opExtrude","CAP_EDGE",EDGE,{"disambiguationData":[OSD([subQ0])],"isStart":false})])]}),makeQuery(id+"F4.opExtrude","CAP_FACE",FACE,{"disambiguationData":[OSD([sQuery(id+"F3.wireOp",EDGE,"E84.MirrorCS"),sQuery(id+"F3.wireOp",EDGE,"E118.MirrorCS"),sQuery(id+"F3.wireOp",EDGE,"E119.MirrorCS"),sQuery(id+"F3.wireOp",EDGE,"E120.MirrorCS")])],"isStart":false})]});}
            var Q35;
            {var subQ0=sQuery(id+"F0.wireOp",EDGE,"E0");Q35=makeQuery(id+"F4.boolean.opBoolean","INTERSECT",EDGE,{"derivedFrom":[makeQuery(id+"F2.opFillet","BLEND_FACE",FACE,{"disambiguationData":[OSD([subQ0]),TDD([makeQuery(id+"F1.opExtrude","CAP_EDGE",EDGE,{"disambiguationData":[OSD([subQ0])],"isStart":false})])]}),makeQuery(id+"F4.opExtrude","CAP_FACE",FACE,{"disambiguationData":[OSD([sQuery(id+"F3.wireOp",EDGE,"E83.MirrorCS"),sQuery(id+"F3.wireOp",EDGE,"E115.MirrorCS"),sQuery(id+"F3.wireOp",EDGE,"E116.MirrorCS"),sQuery(id+"F3.wireOp",EDGE,"E117.MirrorCS")])],"isStart":false})]});}
            var Q36;
            {var subQ0=sQuery(id+"F0.wireOp",EDGE,"E0");Q36=makeQuery(id+"F4.boolean.opBoolean","INTERSECT",EDGE,{"derivedFrom":[makeQuery(id+"F2.opFillet","BLEND_FACE",FACE,{"disambiguationData":[OSD([subQ0]),TDD([makeQuery(id+"F1.opExtrude","CAP_EDGE",EDGE,{"disambiguationData":[OSD([subQ0])],"isStart":false})])]}),makeQuery(id+"F4.opExtrude","CAP_FACE",FACE,{"disambiguationData":[OSD([sQuery(id+"F3.wireOp",EDGE,"E82.MirrorCS"),sQuery(id+"F3.wireOp",EDGE,"E112.MirrorCS"),sQuery(id+"F3.wireOp",EDGE,"E113.MirrorCS"),sQuery(id+"F3.wireOp",EDGE,"E114.MirrorCS")])],"isStart":false})]});}
            var Q37;
            {var subQ0=sQuery(id+"F0.wireOp",EDGE,"E0");Q37=makeQuery(id+"F4.boolean.opBoolean","INTERSECT",EDGE,{"derivedFrom":[makeQuery(id+"F2.opFillet","BLEND_FACE",FACE,{"disambiguationData":[OSD([subQ0]),TDD([makeQuery(id+"F1.opExtrude","CAP_EDGE",EDGE,{"disambiguationData":[OSD([subQ0])],"isStart":false})])]}),makeQuery(id+"F4.opExtrude","CAP_FACE",FACE,{"disambiguationData":[OSD([sQuery(id+"F3.wireOp",EDGE,"E80.MirrorCS"),sQuery(id+"F3.wireOp",EDGE,"E109.MirrorCS"),sQuery(id+"F3.wireOp",EDGE,"E110.MirrorCS"),sQuery(id+"F3.wireOp",EDGE,"E111.MirrorCS")])],"isStart":false})]});}
            var Q38;
            {var subQ0=sQuery(id+"F0.wireOp",EDGE,"E0");Q38=makeQuery(id+"F4.boolean.opBoolean","INTERSECT",EDGE,{"derivedFrom":[makeQuery(id+"F2.opFillet","BLEND_FACE",FACE,{"disambiguationData":[OSD([subQ0]),TDD([makeQuery(id+"F1.opExtrude","CAP_EDGE",EDGE,{"disambiguationData":[OSD([subQ0])],"isStart":false})])]}),makeQuery(id+"F4.opExtrude","CAP_FACE",FACE,{"disambiguationData":[OSD([sQuery(id+"F3.wireOp",EDGE,"E81.MirrorCS"),sQuery(id+"F3.wireOp",EDGE,"E106.MirrorCS"),sQuery(id+"F3.wireOp",EDGE,"E107.MirrorCS"),sQuery(id+"F3.wireOp",EDGE,"E108.MirrorCS")])],"isStart":false})]});}
            var Q39;
            {var subQ0=sQuery(id+"F0.wireOp",EDGE,"E0");Q39=makeQuery(id+"F4.boolean.opBoolean","INTERSECT",EDGE,{"derivedFrom":[makeQuery(id+"F2.opFillet","BLEND_FACE",FACE,{"disambiguationData":[OSD([subQ0]),TDD([makeQuery(id+"F1.opExtrude","CAP_EDGE",EDGE,{"disambiguationData":[OSD([subQ0])],"isStart":false})])]}),makeQuery(id+"F4.opExtrude","CAP_FACE",FACE,{"disambiguationData":[OSD([sQuery(id+"F3.wireOp",EDGE,"E102.MirrorCS"),sQuery(id+"F3.wireOp",EDGE,"E103.MirrorCS"),sQuery(id+"F3.wireOp",EDGE,"E104.MirrorCS"),sQuery(id+"F3.wireOp",EDGE,"E105.MirrorCS")])],"isStart":false})]});}
            var Q40;
            {var subQ0=sQuery(id+"F0.wireOp",EDGE,"E0");Q40=makeQuery(id+"F4.boolean.opBoolean","INTERSECT",EDGE,{"derivedFrom":[makeQuery(id+"F2.opFillet","BLEND_FACE",FACE,{"disambiguationData":[OSD([subQ0]),TDD([makeQuery(id+"F1.opExtrude","CAP_EDGE",EDGE,{"disambiguationData":[OSD([subQ0])],"isStart":false})])]}),makeQuery(id+"F4.opExtrude","CAP_FACE",FACE,{"disambiguationData":[OSD([sQuery(id+"F3.wireOp",EDGE,"E85.MirrorCS"),sQuery(id+"F3.wireOp",EDGE,"E121.MirrorCS"),sQuery(id+"F3.wireOp",EDGE,"E122.MirrorCS"),sQuery(id+"F3.wireOp",EDGE,"E123.MirrorCS")])],"isStart":false})]});}
            chamfer(context, id + "F5", {"entities" : qUnion([Q0, Q1, Q2, Q3, Q4, Q5, Q6, Q7, Q8, Q9, Q10, Q11, Q12, Q13, Q14, Q15, Q16, Q17, Q18, Q19, Q20, Q21, Q22, Q23, Q24, Q25, Q26, Q27, Q28, Q29, Q30, Q31, Q32, Q33, Q34, Q35, Q36, Q37, Q38, Q39, Q40]), "width" : 10.16 * mm, "tangentPropagation" : true});
        }
        {
            var Q0;
            Q0=makeQuery(id+"F4.opExtrude","CAP_EDGE",EDGE,{"disambiguationData":[OSD([sQuery(id+"F3.wireOp",EDGE,"E86.MirrorCS")])],"isStart":true});
            var Q1;
            Q1=makeQuery(id+"F4.opExtrude","CAP_EDGE",EDGE,{"disambiguationData":[OSD([sQuery(id+"F3.wireOp",EDGE,"E85.MirrorCS")])],"isStart":true});
            var Q2;
            Q2=makeQuery(id+"F4.opExtrude","CAP_EDGE",EDGE,{"disambiguationData":[OSD([sQuery(id+"F3.wireOp",EDGE,"E87.MirrorCS")])],"isStart":true});
            var Q3;
            Q3=makeQuery(id+"F4.opExtrude","CAP_EDGE",EDGE,{"disambiguationData":[OSD([sQuery(id+"F3.wireOp",EDGE,"E88.MirrorCS")])],"isStart":true});
            var Q4;
            Q4=makeQuery(id+"F4.opExtrude","CAP_EDGE",EDGE,{"disambiguationData":[OSD([sQuery(id+"F3.wireOp",EDGE,"E89.MirrorCS")])],"isStart":true});
            var Q5;
            Q5=makeQuery(id+"F4.opExtrude","CAP_EDGE",EDGE,{"disambiguationData":[OSD([sQuery(id+"F3.wireOp",EDGE,"E90.MirrorCS")])],"isStart":true});
            var Q6;
            Q6=makeQuery(id+"F4.opExtrude","CAP_EDGE",EDGE,{"disambiguationData":[OSD([sQuery(id+"F3.wireOp",EDGE,"E91.MirrorCS")])],"isStart":true});
            var Q7;
            Q7=makeQuery(id+"F4.opExtrude","CAP_EDGE",EDGE,{"disambiguationData":[OSD([sQuery(id+"F3.wireOp",EDGE,"E92.MirrorCS")])],"isStart":true});
            var Q8;
            Q8=makeQuery(id+"F4.opExtrude","CAP_EDGE",EDGE,{"disambiguationData":[OSD([sQuery(id+"F3.wireOp",EDGE,"E93.MirrorCS")])],"isStart":true});
            var Q9;
            Q9=makeQuery(id+"F4.opExtrude","CAP_EDGE",EDGE,{"disambiguationData":[OSD([sQuery(id+"F3.wireOp",EDGE,"E94.MirrorCS")])],"isStart":true});
            var Q10;
            Q10=makeQuery(id+"F4.opExtrude","CAP_EDGE",EDGE,{"disambiguationData":[OSD([sQuery(id+"F3.wireOp",EDGE,"E95.MirrorCS")])],"isStart":true});
            var Q11;
            Q11=makeQuery(id+"F4.opExtrude","CAP_EDGE",EDGE,{"disambiguationData":[OSD([sQuery(id+"F3.wireOp",EDGE,"E96.MirrorCS")])],"isStart":true});
            var Q12;
            Q12=makeQuery(id+"F4.opExtrude","CAP_EDGE",EDGE,{"disambiguationData":[OSD([sQuery(id+"F3.wireOp",EDGE,"E97.MirrorCS")])],"isStart":true});
            var Q13;
            Q13=makeQuery(id+"F4.opExtrude","CAP_EDGE",EDGE,{"disambiguationData":[OSD([sQuery(id+"F3.wireOp",EDGE,"E98.MirrorCS")])],"isStart":true});
            var Q14;
            Q14=makeQuery(id+"F4.opExtrude","CAP_EDGE",EDGE,{"disambiguationData":[OSD([sQuery(id+"F3.wireOp",EDGE,"E99.MirrorCS")])],"isStart":true});
            var Q15;
            Q15=makeQuery(id+"F4.opExtrude","CAP_EDGE",EDGE,{"disambiguationData":[OSD([sQuery(id+"F3.wireOp",EDGE,"E43.MirrorCS")])],"isStart":true});
            var Q16;
            Q16=makeQuery(id+"F4.opExtrude","CAP_EDGE",EDGE,{"disambiguationData":[OSD([sQuery(id+"F3.wireOp",EDGE,"E46.MirrorCS")])],"isStart":true});
            var Q17;
            Q17=makeQuery(id+"F4.opExtrude","CAP_EDGE",EDGE,{"disambiguationData":[OSD([sQuery(id+"F3.wireOp",EDGE,"E50.MirrorCS")])],"isStart":true});
            var Q18;
            Q18=makeQuery(id+"F4.opExtrude","CAP_EDGE",EDGE,{"disambiguationData":[OSD([sQuery(id+"F3.wireOp",EDGE,"E54.MirrorCS")])],"isStart":true});
            var Q19;
            Q19=makeQuery(id+"F4.opExtrude","CAP_EDGE",EDGE,{"disambiguationData":[OSD([sQuery(id+"F3.wireOp",EDGE,"E55.MirrorCS")])],"isStart":true});
            var Q20;
            Q20=makeQuery(id+"F4.opExtrude","CAP_EDGE",EDGE,{"disambiguationData":[OSD([sQuery(id+"F3.wireOp",EDGE,"E56.MirrorCS")])],"isStart":true});
            var Q21;
            Q21=makeQuery(id+"F4.opExtrude","CAP_EDGE",EDGE,{"disambiguationData":[OSD([sQuery(id+"F3.wireOp",EDGE,"E57.MirrorCS")])],"isStart":true});
            var Q22;
            Q22=makeQuery(id+"F4.opExtrude","CAP_EDGE",EDGE,{"disambiguationData":[OSD([sQuery(id+"F3.wireOp",EDGE,"E68.MirrorCS")])],"isStart":true});
            var Q23;
            Q23=makeQuery(id+"F4.opExtrude","CAP_EDGE",EDGE,{"disambiguationData":[OSD([sQuery(id+"F3.wireOp",EDGE,"E72.MirrorCS")])],"isStart":true});
            var Q24;
            Q24=makeQuery(id+"F4.opExtrude","CAP_EDGE",EDGE,{"disambiguationData":[OSD([sQuery(id+"F3.wireOp",EDGE,"E76.MirrorCS")])],"isStart":true});
            var Q25;
            Q25=makeQuery(id+"F4.opExtrude","CAP_EDGE",EDGE,{"disambiguationData":[OSD([sQuery(id+"F3.wireOp",EDGE,"E32.MirrorCS")])],"isStart":true});
            var Q26;
            Q26=makeQuery(id+"F4.opExtrude","CAP_EDGE",EDGE,{"disambiguationData":[OSD([sQuery(id+"F3.wireOp",EDGE,"E31.MirrorCS")])],"isStart":true});
            var Q27;
            Q27=makeQuery(id+"F4.opExtrude","CAP_EDGE",EDGE,{"disambiguationData":[OSD([sQuery(id+"F3.wireOp",EDGE,"E30.MirrorCS")])],"isStart":true});
            var Q28;
            Q28=makeQuery(id+"F4.opExtrude","CAP_EDGE",EDGE,{"disambiguationData":[OSD([sQuery(id+"F3.wireOp",EDGE,"E26.MirrorCS")])],"isStart":true});
            var Q29;
            Q29=makeQuery(id+"F4.opExtrude","CAP_EDGE",EDGE,{"disambiguationData":[OSD([sQuery(id+"F3.wireOp",EDGE,"E22.MirrorCS")])],"isStart":true});
            var Q30;
            Q30=makeQuery(id+"F4.opExtrude","CAP_EDGE",EDGE,{"disambiguationData":[OSD([sQuery(id+"F3.wireOp",EDGE,"E18.MirrorCS")])],"isStart":true});
            var Q31;
            Q31=makeQuery(id+"F4.opExtrude","CAP_EDGE",EDGE,{"disambiguationData":[OSD([sQuery(id+"F3.wireOp",EDGE,"E15.MirrorCS")])],"isStart":true});
            var Q32;
            Q32=makeQuery(id+"F4.opExtrude","CAP_EDGE",EDGE,{"disambiguationData":[OSD([sQuery(id+"F3.wireOp",EDGE,"E10.MirrorCS")])],"isStart":true});
            var Q33;
            Q33=makeQuery(id+"F4.opExtrude","CAP_EDGE",EDGE,{"disambiguationData":[OSD([sQuery(id+"F3.wireOp",EDGE,"E8.MirrorCS")])],"isStart":true});
            var Q34;
            Q34=makeQuery(id+"F4.opExtrude","CAP_EDGE",EDGE,{"disambiguationData":[OSD([sQuery(id+"F3.wireOp",EDGE,"E5")])],"isStart":true});
            var Q35;
            Q35=makeQuery(id+"F4.opExtrude","CAP_EDGE",EDGE,{"disambiguationData":[OSD([sQuery(id+"F3.wireOp",EDGE,"E102.MirrorCS")])],"isStart":true});
            var Q36;
            Q36=makeQuery(id+"F4.opExtrude","CAP_EDGE",EDGE,{"disambiguationData":[OSD([sQuery(id+"F3.wireOp",EDGE,"E81.MirrorCS")])],"isStart":true});
            var Q37;
            Q37=makeQuery(id+"F4.opExtrude","CAP_EDGE",EDGE,{"disambiguationData":[OSD([sQuery(id+"F3.wireOp",EDGE,"E80.MirrorCS")])],"isStart":true});
            var Q38;
            Q38=makeQuery(id+"F4.opExtrude","CAP_EDGE",EDGE,{"disambiguationData":[OSD([sQuery(id+"F3.wireOp",EDGE,"E82.MirrorCS")])],"isStart":true});
            var Q39;
            Q39=makeQuery(id+"F4.opExtrude","CAP_EDGE",EDGE,{"disambiguationData":[OSD([sQuery(id+"F3.wireOp",EDGE,"E83.MirrorCS")])],"isStart":true});
            var Q40;
            Q40=makeQuery(id+"F4.opExtrude","CAP_EDGE",EDGE,{"disambiguationData":[OSD([sQuery(id+"F3.wireOp",EDGE,"E84.MirrorCS")])],"isStart":true});
            fillet(context, id + "F6", {"entities" : qUnion([Q0, Q1, Q2, Q3, Q4, Q5, Q6, Q7, Q8, Q9, Q10, Q11, Q12, Q13, Q14, Q15, Q16, Q17, Q18, Q19, Q20, Q21, Q22, Q23, Q24, Q25, Q26, Q27, Q28, Q29, Q30, Q31, Q32, Q33, Q34, Q35, Q36, Q37, Q38, Q39, Q40]), "radius" : 2.54 * mm, "tangentPropagation" : true, "allowEdgeOverflow" : false});
        }
        {
            var Q0;
            Q0=makeQuery(id+"F1.opExtrude","CAP_EDGE",EDGE,{"disambiguationData":[OSD([sQuery(id+"F0.wireOp",EDGE,"E1")])],"isStart":false});
            var Q1;
            Q1=makeQuery(id+"F1.opExtrude","CAP_EDGE",EDGE,{"disambiguationData":[OSD([sQuery(id+"F0.wireOp",EDGE,"E1")])],"isStart":true});
            fillet(context, id + "F7", {"entities" : qUnion([Q0, Q1]), "radius" : 12.7 * mm, "tangentPropagation" : true, "allowEdgeOverflow" : false});
        }
        {
            var Q0;
            Q0=qCreatedBy(makeId("Front.planeOp"),FACE);
            var sketch = newSketch(context, id + "F8", { "sketchPlane" : qUnion([Q0])});
            skArc(sketch, "E166", {"start": v(83.5, 319.43) * mm, "mid": v(72.6, 330.21) * mm, "end": v(58.2, 325) * mm});
            skArc(sketch, "E167", {"start": v(58.2, 325) * mm, "mid": v(69.53, 316.2) * mm, "end": v(83.5, 319.43) * mm});
            skSolve(sketch);
        }
        {
            var Q0;
            Q0 = qSketchRegion(id + "F8", true);
            extrude(context, id + "F9", {"entities" : qUnion([Q0]), "operationType" : NewBodyOperationType.ADD, "oppositeDirection" : true, "depth" : 20.32 * mm});
        }
        {
            var Q0;
            {var subQ0=sQuery(id+"F0.wireOp",EDGE,"E0");Q0=makeQuery(id+"F9.boolean.opBoolean","INTERSECT",EDGE,{"derivedFrom":[makeQuery(id+"F2.opFillet","BLEND_FACE",FACE,{"disambiguationData":[OSD([subQ0]),TDD([makeQuery(id+"F1.opExtrude","CAP_EDGE",EDGE,{"disambiguationData":[OSD([subQ0])],"isStart":true})])]}),makeQuery(id+"F9.opExtrude","CAP_FACE",FACE,{"disambiguationData":[OSD([sQuery(id+"F8.wireOp",EDGE,"E166"),sQuery(id+"F8.wireOp",EDGE,"E167")])],"isStart":false})]});}
            chamfer(context, id + "F10", {"entities" : qUnion([Q0]), "width" : 10.16 * mm, "tangentPropagation" : true});
        }
        {
            var Q0;
            Q0=makeQuery(id+"F9.opExtrude","CAP_EDGE",EDGE,{"disambiguationData":[OSD([sQuery(id+"F8.wireOp",EDGE,"E166")])],"isStart":true});
            fillet(context, id + "F11", {"entities" : qUnion([Q0]), "radius" : 2.54 * mm, "tangentPropagation" : true, "allowEdgeOverflow" : false});
        }
        {
            var Q0;
            Q0=qCreatedBy(makeId("Top.planeOp"),FACE);
            var sketch = newSketch(context, id + "F12", { "sketchPlane" : qUnion([Q0])});
            skLineSegment(sketch, "E168", {"start": v(0, 90.49) * mm, "end": v(0, -90.49) * mm});
            skSolve(sketch);
        }
    });
